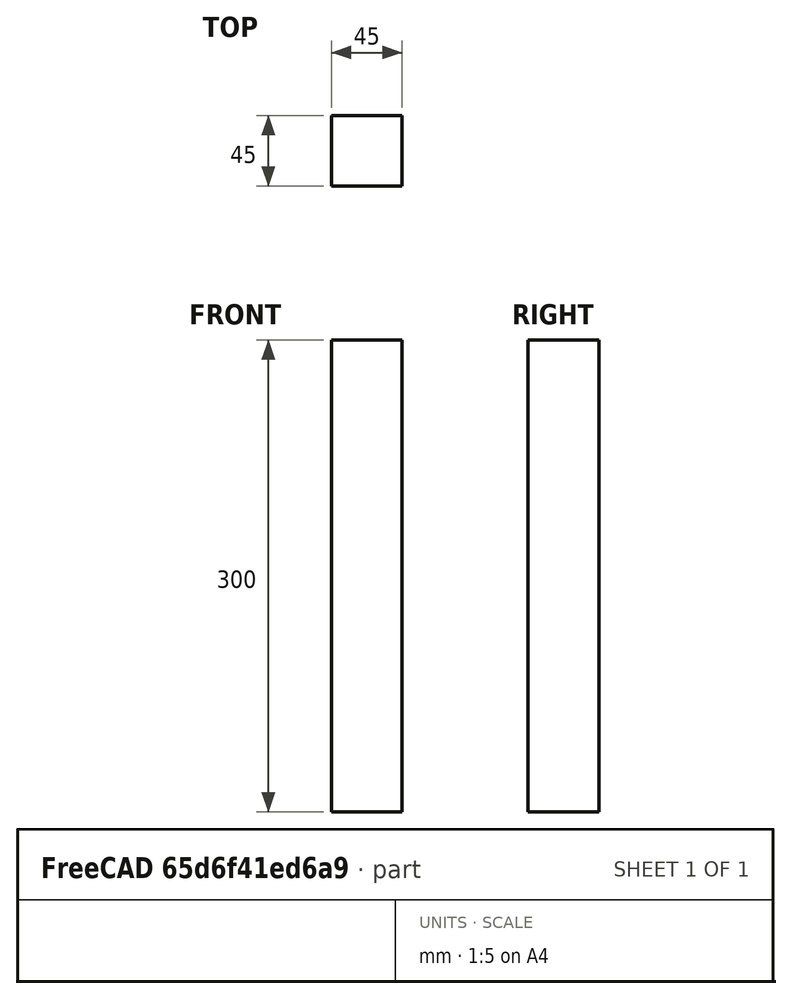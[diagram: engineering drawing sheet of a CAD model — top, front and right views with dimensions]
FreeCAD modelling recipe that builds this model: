
FCSTD DOCUMENT  (FreeCAD 0.18R4 (GitTag))
Label: glue_block
License: All rights reserved
LicenseURL: http://en.wikipedia.org/wiki/All_rights_reserved
objects: Sketcher::SketchObject×1, PartDesign::Pad×1, PartDesign::Body×1
note: 4 computed .brp shape members not serialized (recipe doc carries the construction recipe); baked Part::Feature solids carry a one-line shape summary decoded from their .brp

FEATURE [Sketcher::SketchObject] Sketch
  MapMode = 5
  Support = -> [XY_Plane]
  sketch-geometry (4):
    g0: LineSegment StartX=0 StartY=0 StartZ=0 EndX=-45 EndY=0 EndZ=0
    g1: LineSegment StartX=-45 StartY=0 StartZ=0 EndX=-45 EndY=45 EndZ=0
    g2: LineSegment StartX=-45 StartY=45 StartZ=0 EndX=0 EndY=45 EndZ=0
    g3: LineSegment StartX=0 StartY=45 StartZ=0 EndX=0 EndY=0 EndZ=0
  constraints (11):
    c: Coincident(g0,g1)
    c: Coincident(g1,g2)
    c: Coincident(g2,g3)
    c: Coincident(g3,g0)
    c: Horizontal(g0)
    c: Horizontal(g2)
    c: Vertical(g1)
    c: Vertical(g3)
    c: Coincident(g0,g-1)
    c: DistanceX(g0,g0) = 45
    c: DistanceY(g3,g3) = 45
FEATURE [PartDesign::Pad] Pad
  Length = 300
  Length2 = 100
  Profile = -> Sketch
  Type = 0
FEATURE [PartDesign::Body] Body
  Group = -> [Sketch,Pad]
  Origin = -> Origin
  Tip = -> Pad
